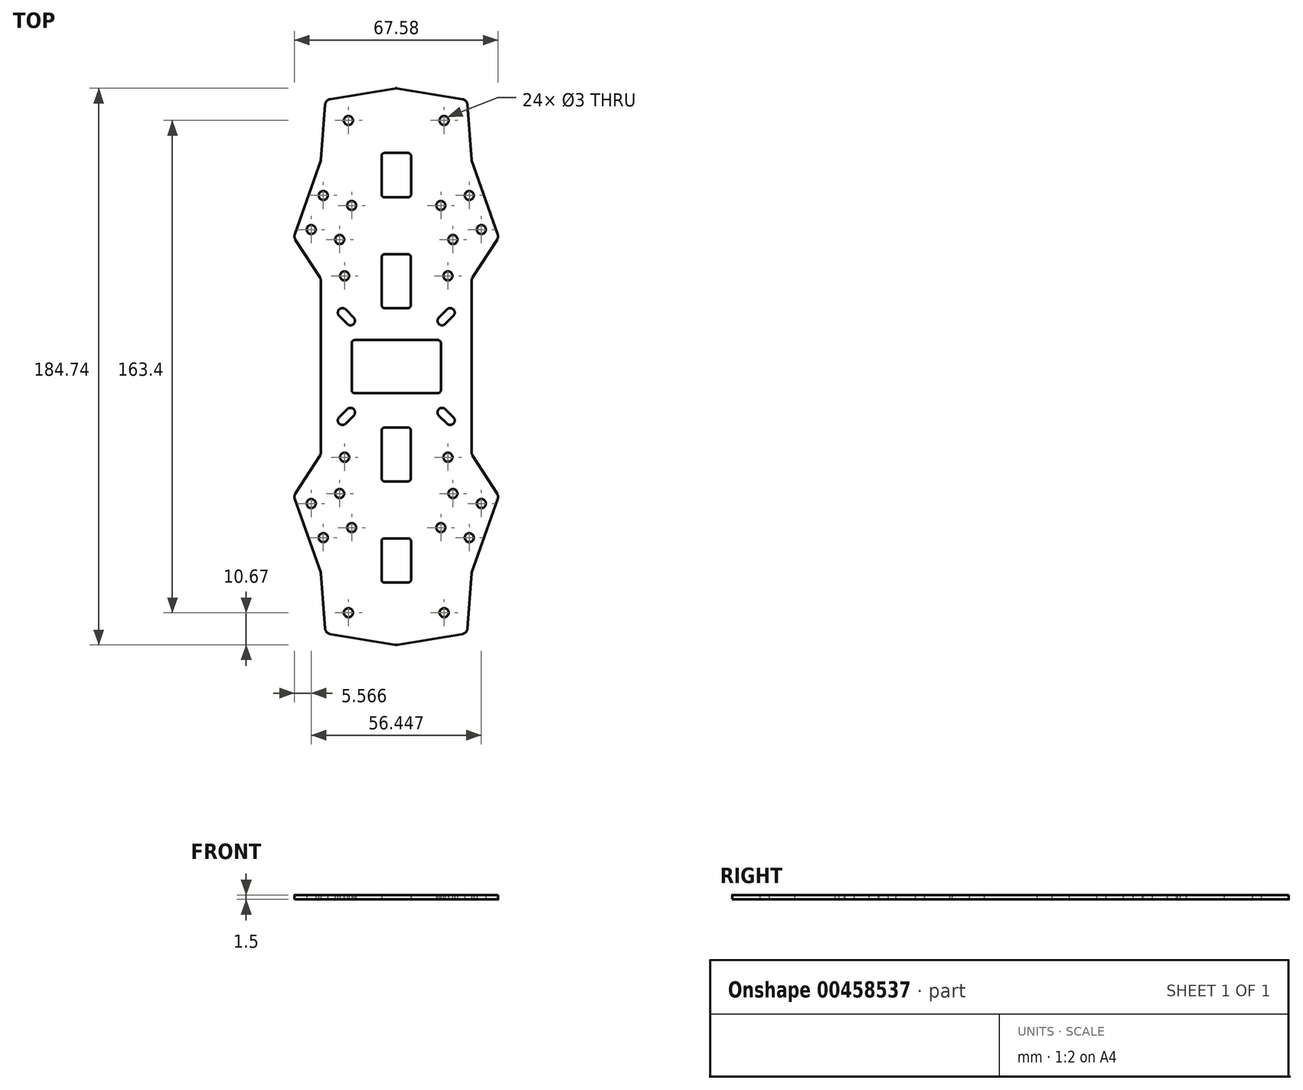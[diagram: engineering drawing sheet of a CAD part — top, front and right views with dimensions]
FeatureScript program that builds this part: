
annotation { "Feature Type Name" : "Feature", "Feature Type Description" : "" }
export const myFeature = defineFeature(function(context is Context, id is Id, definition is map)
    precondition{}
    {
        {
            var Q0;
            Q0=qCreatedBy(makeId("Top.planeOp"),FACE);
            var sketch = newSketch(context, id + "F0", { "sketchPlane" : qUnion([Q0])});
            skLineSegment(sketch, "E0", {"start": v(-25, 28.41) * mm, "end": v(-25, -28.41) * mm});
            skLineSegment(sketch, "E1", {"start": v(-25.32, -29.5) * mm, "end": v(-33.47, -42.18) * mm});
            skLineSegment(sketch, "E2", {"start": v(-33.67, -43.92) * mm, "end": v(-25.04, -68.37) * mm});
            skLineSegment(sketch, "E3", {"start": v(-25, -68.63) * mm, "end": v(-23.62, -86.93) * mm});
            skLineSegment(sketch, "E4", {"start": v(-21.95, -88.76) * mm, "end": v(-0.33, -92.35) * mm});
            skLineSegment(sketch, "E5", {"start": v(0.33, -92.35) * mm, "end": v(21.95, -88.76) * mm});
            skLineSegment(sketch, "E6", {"start": v(23.62, -86.93) * mm, "end": v(25, -68.63) * mm});
            skLineSegment(sketch, "E7", {"start": v(25.04, -68.37) * mm, "end": v(33.67, -43.92) * mm});
            skLineSegment(sketch, "E8", {"start": v(33.47, -42.18) * mm, "end": v(25.32, -29.5) * mm});
            skLineSegment(sketch, "E9", {"start": v(25, -28.41) * mm, "end": v(25, 28.41) * mm});
            skLineSegment(sketch, "E10", {"start": v(25.32, 29.5) * mm, "end": v(33.47, 42.18) * mm});
            skLineSegment(sketch, "E11", {"start": v(33.67, 43.92) * mm, "end": v(25.04, 68.37) * mm});
            skLineSegment(sketch, "E12", {"start": v(25, 68.63) * mm, "end": v(23.62, 86.93) * mm});
            skLineSegment(sketch, "E13", {"start": v(21.95, 88.76) * mm, "end": v(0.33, 92.35) * mm});
            skLineSegment(sketch, "E14", {"start": v(-0.33, 92.35) * mm, "end": v(-21.95, 88.76) * mm});
            skLineSegment(sketch, "E15", {"start": v(-23.62, 86.93) * mm, "end": v(-25, 68.63) * mm});
            skLineSegment(sketch, "E16", {"start": v(-25.04, 68.37) * mm, "end": v(-33.67, 43.92) * mm});
            skLineSegment(sketch, "E17", {"start": v(-33.47, 42.18) * mm, "end": v(-25.32, 29.5) * mm});
            skLineSegment(sketch, "E18.bottom", {"start": v(-13.8, 8.8) * mm, "end": v(13.8, 8.8) * mm});
            skLineSegment(sketch, "E18.top", {"start": v(-13.8, -8.8) * mm, "end": v(13.8, -8.8) * mm});
            skLineSegment(sketch, "E18.left", {"start": v(-14.8, 7.8) * mm, "end": v(-14.8, -7.8) * mm});
            skLineSegment(sketch, "E18.right", {"start": v(14.8, 7.8) * mm, "end": v(14.8, -7.8) * mm});
            skPoint(sketch, "E18.middle", {"position": v(0, 0) * mm});
            skPoint(sketch, "E19.visualSharp", {"position": v(-14.8, 8.8) * mm});
            skArc(sketch, "E19.filletArc", {"start": v(-13.8, 8.8) * mm, "mid": v(-14.5, 8.5) * mm, "end": v(-14.8, 7.8) * mm});
            skPoint(sketch, "E20.visualSharp", {"position": v(14.8, 8.8) * mm});
            skArc(sketch, "E20.filletArc", {"start": v(14.8, 7.8) * mm, "mid": v(14.5, 8.5) * mm, "end": v(13.8, 8.8) * mm});
            skPoint(sketch, "E21.visualSharp", {"position": v(14.8, -8.8) * mm});
            skArc(sketch, "E21.filletArc", {"start": v(13.8, -8.8) * mm, "mid": v(14.5, -8.5) * mm, "end": v(14.8, -7.8) * mm});
            skPoint(sketch, "E22.visualSharp", {"position": v(-14.8, -8.8) * mm});
            skArc(sketch, "E22.filletArc", {"start": v(-14.8, -7.8) * mm, "mid": v(-14.5, -8.5) * mm, "end": v(-13.8, -8.8) * mm});
            skLineSegment(sketch, "E23.bottom", {"start": v(-3.85, 19.4) * mm, "end": v(3.85, 19.4) * mm});
            skLineSegment(sketch, "E23.top", {"start": v(-3.85, 37.3) * mm, "end": v(3.85, 37.3) * mm});
            skLineSegment(sketch, "E23.left", {"start": v(-4.85, 20.4) * mm, "end": v(-4.85, 36.3) * mm});
            skLineSegment(sketch, "E23.right", {"start": v(4.85, 20.4) * mm, "end": v(4.85, 36.3) * mm});
            skPoint(sketch, "E23.middle", {"position": v(0, 28.35) * mm});
            skPoint(sketch, "E24.visualSharp", {"position": v(-4.85, 37.3) * mm});
            skArc(sketch, "E24.filletArc", {"start": v(-3.85, 37.3) * mm, "mid": v(-4.56, 37) * mm, "end": v(-4.85, 36.3) * mm});
            skPoint(sketch, "E25.visualSharp", {"position": v(4.85, 37.3) * mm});
            skArc(sketch, "E25.filletArc", {"start": v(4.85, 36.3) * mm, "mid": v(4.56, 37) * mm, "end": v(3.85, 37.3) * mm});
            skPoint(sketch, "E26.visualSharp", {"position": v(4.85, 19.4) * mm});
            skArc(sketch, "E26.filletArc", {"start": v(3.85, 19.4) * mm, "mid": v(4.56, 19.7) * mm, "end": v(4.85, 20.4) * mm});
            skPoint(sketch, "E27.visualSharp", {"position": v(-4.85, 19.4) * mm});
            skArc(sketch, "E27.filletArc", {"start": v(-4.85, 20.4) * mm, "mid": v(-4.56, 19.7) * mm, "end": v(-3.85, 19.4) * mm});
            skLineSegment(sketch, "E28.bottom", {"start": v(-3.9, 56.2) * mm, "end": v(3.9, 56.2) * mm});
            skLineSegment(sketch, "E28.top", {"start": v(-3.9, 70.9) * mm, "end": v(3.9, 70.9) * mm});
            skLineSegment(sketch, "E28.left", {"start": v(-4.9, 57.2) * mm, "end": v(-4.9, 69.9) * mm});
            skLineSegment(sketch, "E28.right", {"start": v(4.9, 57.2) * mm, "end": v(4.9, 69.9) * mm});
            skPoint(sketch, "E28.middle", {"position": v(0, 63.55) * mm});
            skPoint(sketch, "E29.visualSharp", {"position": v(4.9, 56.2) * mm});
            skArc(sketch, "E29.filletArc", {"start": v(3.9, 56.2) * mm, "mid": v(4.6, 56.5) * mm, "end": v(4.9, 57.2) * mm});
            skPoint(sketch, "E30.visualSharp", {"position": v(-4.9, 56.2) * mm});
            skArc(sketch, "E30.filletArc", {"start": v(-4.9, 57.2) * mm, "mid": v(-4.6, 56.5) * mm, "end": v(-3.9, 56.2) * mm});
            skPoint(sketch, "E31.visualSharp", {"position": v(-4.9, 70.9) * mm});
            skArc(sketch, "E31.filletArc", {"start": v(-3.9, 70.9) * mm, "mid": v(-4.6, 70.6) * mm, "end": v(-4.9, 69.9) * mm});
            skPoint(sketch, "E32.visualSharp", {"position": v(4.9, 70.9) * mm});
            skArc(sketch, "E32.filletArc", {"start": v(4.9, 69.9) * mm, "mid": v(4.6, 70.6) * mm, "end": v(3.9, 70.9) * mm});
            skPoint(sketch, "E33.visualSharp", {"position": v(-34, -43) * mm});
            skArc(sketch, "E33.filletArc", {"start": v(-33.47, -42.18) * mm, "mid": v(-33.77, -43.03) * mm, "end": v(-33.67, -43.92) * mm});
            skPoint(sketch, "E34.visualSharp", {"position": v(34, -43) * mm});
            skArc(sketch, "E34.filletArc", {"start": v(33.67, -43.92) * mm, "mid": v(33.77, -43.03) * mm, "end": v(33.47, -42.18) * mm});
            skPoint(sketch, "E35.visualSharp", {"position": v(25, -29) * mm});
            skArc(sketch, "E35.filletArc", {"start": v(25, -28.41) * mm, "mid": v(25.08, -28.98) * mm, "end": v(25.32, -29.5) * mm});
            skPoint(sketch, "E36.visualSharp", {"position": v(-25, -29) * mm});
            skArc(sketch, "E36.filletArc", {"start": v(-25.32, -29.5) * mm, "mid": v(-25.08, -28.98) * mm, "end": v(-25, -28.41) * mm});
            skPoint(sketch, "E37.visualSharp", {"position": v(-25, -68.5) * mm});
            skArc(sketch, "E37.filletArc", {"start": v(-25, -68.63) * mm, "mid": v(-25, -68.5) * mm, "end": v(-25.04, -68.37) * mm});
            skPoint(sketch, "E38.visualSharp", {"position": v(25, -68.5) * mm});
            skArc(sketch, "E38.filletArc", {"start": v(25.04, -68.37) * mm, "mid": v(25, -68.5) * mm, "end": v(25, -68.63) * mm});
            skPoint(sketch, "E39.visualSharp", {"position": v(23.5, -88.5) * mm});
            skArc(sketch, "E39.filletArc", {"start": v(21.95, -88.76) * mm, "mid": v(23.1, -88.13) * mm, "end": v(23.62, -86.93) * mm});
            skPoint(sketch, "E40.visualSharp", {"position": v(-23.5, -88.5) * mm});
            skArc(sketch, "E40.filletArc", {"start": v(-23.62, -86.93) * mm, "mid": v(-23.1, -88.13) * mm, "end": v(-21.95, -88.76) * mm});
            skPoint(sketch, "E41.visualSharp", {"position": v(0, -92.4) * mm});
            skArc(sketch, "E41.filletArc", {"start": v(-0.33, -92.35) * mm, "mid": v(0, -92.37) * mm, "end": v(0.33, -92.35) * mm});
            skPoint(sketch, "E42.visualSharp", {"position": v(25, 29) * mm});
            skArc(sketch, "E42.filletArc", {"start": v(25.32, 29.5) * mm, "mid": v(25.08, 28.98) * mm, "end": v(25, 28.41) * mm});
            skPoint(sketch, "E43.visualSharp", {"position": v(-25, 29) * mm});
            skArc(sketch, "E43.filletArc", {"start": v(-25, 28.41) * mm, "mid": v(-25.08, 28.98) * mm, "end": v(-25.32, 29.5) * mm});
            skPoint(sketch, "E44.visualSharp", {"position": v(34, 43) * mm});
            skArc(sketch, "E44.filletArc", {"start": v(33.47, 42.18) * mm, "mid": v(33.77, 43.03) * mm, "end": v(33.67, 43.92) * mm});
            skPoint(sketch, "E45.visualSharp", {"position": v(-34, 43) * mm});
            skArc(sketch, "E45.filletArc", {"start": v(-33.67, 43.92) * mm, "mid": v(-33.77, 43.03) * mm, "end": v(-33.47, 42.18) * mm});
            skPoint(sketch, "E46.visualSharp", {"position": v(-25, 68.5) * mm});
            skArc(sketch, "E46.filletArc", {"start": v(-25.04, 68.37) * mm, "mid": v(-25, 68.5) * mm, "end": v(-25, 68.63) * mm});
            skPoint(sketch, "E47.visualSharp", {"position": v(25, 68.5) * mm});
            skArc(sketch, "E47.filletArc", {"start": v(25, 68.63) * mm, "mid": v(25, 68.5) * mm, "end": v(25.04, 68.37) * mm});
            skPoint(sketch, "E48.visualSharp", {"position": v(23.5, 88.5) * mm});
            skArc(sketch, "E48.filletArc", {"start": v(23.62, 86.93) * mm, "mid": v(23.1, 88.13) * mm, "end": v(21.95, 88.76) * mm});
            skPoint(sketch, "E49.visualSharp", {"position": v(-23.5, 88.5) * mm});
            skArc(sketch, "E49.filletArc", {"start": v(-21.95, 88.76) * mm, "mid": v(-23.1, 88.13) * mm, "end": v(-23.62, 86.93) * mm});
            skPoint(sketch, "E50.visualSharp", {"position": v(0, 92.4) * mm});
            skArc(sketch, "E50.filletArc", {"start": v(0.33, 92.35) * mm, "mid": v(0, 92.37) * mm, "end": v(-0.33, 92.35) * mm});
            skArc(sketch, "E51.MirrorCS", {"start": v(4.85, 20.4) * mm, "mid": v(4.56, 19.7) * mm, "end": v(3.85, 19.4) * mm});
            skArc(sketch, "E52.MirrorCS", {"start": v(-3.85, 19.4) * mm, "mid": v(-4.56, 19.7) * mm, "end": v(-4.85, 20.4) * mm});
            skLineSegment(sketch, "E53.MirrorCS", {"start": v(3.85, 19.4) * mm, "end": v(-3.85, 19.4) * mm});
            skCircle(sketch, "E54", {"center": v(-17.15, 30.1) * mm, "radius": 1.5 * mm});
            skCircle(sketch, "E55.MirrorC", {"center": v(-17.15, -30.1) * mm, "radius": 1.5 * mm});
            skCircle(sketch, "E56.MirrorC", {"center": v(17.15, -30.1) * mm, "radius": 1.5 * mm});
            skCircle(sketch, "E57.MirrorC", {"center": v(17.15, 30.1) * mm, "radius": 1.5 * mm});
            skCircle(sketch, "E58", {"center": v(-15.88, 81.7) * mm, "radius": 1.5 * mm});
            skCircle(sketch, "E59.MirrorC", {"center": v(15.88, 81.7) * mm, "radius": 1.5 * mm});
            skCircle(sketch, "E60.MirrorC", {"center": v(15.88, -81.7) * mm, "radius": 1.5 * mm});
            skCircle(sketch, "E61.MirrorC", {"center": v(-15.88, -81.7) * mm, "radius": 1.5 * mm});
            skLineSegment(sketch, "E62", {"start": v(-17.89, 17.89) * mm, "end": v(-15.2, 15.2) * mm});
            skArc(sketch, "E63.0.startCap", {"start": v(-18.95, 16.83) * mm, "mid": v(-18.95, 18.95) * mm, "end": v(-16.83, 18.95) * mm});
            skArc(sketch, "E63.0.endCap", {"start": v(-14.14, 16.26) * mm, "mid": v(-14.14, 14.14) * mm, "end": v(-16.26, 14.14) * mm});
            skLineSegment(sketch, "E63.0.left", {"start": v(-16.83, 18.95) * mm, "end": v(-14.14, 16.26) * mm});
            skLineSegment(sketch, "E63.0.right", {"start": v(-18.95, 16.83) * mm, "end": v(-16.26, 14.14) * mm});
            skLineSegment(sketch, "E64.MirrorCS", {"start": v(18.95, 16.83) * mm, "end": v(16.26, 14.14) * mm});
            skLineSegment(sketch, "E65.MirrorCS", {"start": v(17.89, 17.89) * mm, "end": v(15.2, 15.2) * mm});
            skLineSegment(sketch, "E66.MirrorCS", {"start": v(16.83, 18.95) * mm, "end": v(14.14, 16.26) * mm});
            skArc(sketch, "E67.MirrorCS", {"start": v(18.95, 16.83) * mm, "mid": v(18.95, 18.95) * mm, "end": v(16.83, 18.95) * mm});
            skArc(sketch, "E68.MirrorCS", {"start": v(14.14, 16.26) * mm, "mid": v(14.14, 14.14) * mm, "end": v(16.26, 14.14) * mm});
            skLineSegment(sketch, "E69.MirrorCS", {"start": v(-16.83, -18.95) * mm, "end": v(-14.14, -16.26) * mm});
            skLineSegment(sketch, "E70.MirrorCS", {"start": v(-17.89, -17.89) * mm, "end": v(-15.2, -15.2) * mm});
            skArc(sketch, "E71.MirrorCS", {"start": v(-14.14, -16.26) * mm, "mid": v(-14.14, -14.14) * mm, "end": v(-16.26, -14.14) * mm});
            skLineSegment(sketch, "E72.MirrorCS", {"start": v(-18.95, -16.83) * mm, "end": v(-16.26, -14.14) * mm});
            skArc(sketch, "E73.MirrorCS", {"start": v(-18.95, -16.83) * mm, "mid": v(-18.95, -18.95) * mm, "end": v(-16.83, -18.95) * mm});
            skLineSegment(sketch, "E74.MirrorCS", {"start": v(17.89, -17.89) * mm, "end": v(15.2, -15.2) * mm});
            skLineSegment(sketch, "E75.MirrorCS", {"start": v(18.95, -16.83) * mm, "end": v(16.26, -14.14) * mm});
            skLineSegment(sketch, "E76.MirrorCS", {"start": v(16.83, -18.95) * mm, "end": v(14.14, -16.26) * mm});
            skArc(sketch, "E77.MirrorCS", {"start": v(18.95, -16.83) * mm, "mid": v(18.95, -18.95) * mm, "end": v(16.83, -18.95) * mm});
            skArc(sketch, "E78.MirrorCS", {"start": v(14.14, -16.26) * mm, "mid": v(14.14, -14.14) * mm, "end": v(16.26, -14.14) * mm});
            skLineSegment(sketch, "E79", {"start": v(-24.34, 50.47) * mm, "end": v(-21.51, 49.47) * mm});
            skLineSegment(sketch, "E80", {"start": v(-21.51, 49.47) * mm, "end": v(-20.51, 52.3) * mm});
            skCircle(sketch, "E81", {"center": v(-18.8, 42.15) * mm, "radius": 1.5 * mm});
            skCircle(sketch, "E82.MirrorC", {"center": v(-14.8, 53.47) * mm, "radius": 1.5 * mm});
            skCircle(sketch, "E83.MirrorC", {"center": v(-24.23, 56.8) * mm, "radius": 1.5 * mm});
            skCircle(sketch, "E84.MirrorC", {"center": v(-28.22, 45.48) * mm, "radius": 1.5 * mm});
            skCircle(sketch, "E85.MirrorC", {"center": v(14.8, 53.47) * mm, "radius": 1.5 * mm});
            skCircle(sketch, "E86.MirrorC", {"center": v(24.23, 56.8) * mm, "radius": 1.5 * mm});
            skCircle(sketch, "E87.MirrorC", {"center": v(28.22, 45.48) * mm, "radius": 1.5 * mm});
            skLineSegment(sketch, "E88.MirrorCS", {"start": v(24.34, 50.47) * mm, "end": v(21.51, 49.47) * mm});
            skLineSegment(sketch, "E89.MirrorCS", {"start": v(21.51, 49.47) * mm, "end": v(20.51, 52.3) * mm});
            skCircle(sketch, "E90.MirrorC", {"center": v(18.8, 42.15) * mm, "radius": 1.5 * mm});
            skLineSegment(sketch, "E91.MirrorCS", {"start": v(21.51, -49.47) * mm, "end": v(20.51, -52.3) * mm});
            skLineSegment(sketch, "E92.MirrorCS", {"start": v(24.34, -50.47) * mm, "end": v(21.51, -49.47) * mm});
            skCircle(sketch, "E93.MirrorC", {"center": v(24.23, -56.8) * mm, "radius": 1.5 * mm});
            skCircle(sketch, "E94.MirrorC", {"center": v(28.22, -45.48) * mm, "radius": 1.5 * mm});
            skCircle(sketch, "E95.MirrorC", {"center": v(18.8, -42.15) * mm, "radius": 1.5 * mm});
            skCircle(sketch, "E96.MirrorC", {"center": v(14.8, -53.47) * mm, "radius": 1.5 * mm});
            skCircle(sketch, "E97.MirrorC", {"center": v(-18.8, -42.15) * mm, "radius": 1.5 * mm});
            skCircle(sketch, "E98.MirrorC", {"center": v(-28.22, -45.48) * mm, "radius": 1.5 * mm});
            skLineSegment(sketch, "E99.MirrorCS", {"start": v(-21.51, -49.47) * mm, "end": v(-20.51, -52.3) * mm});
            skLineSegment(sketch, "E100.MirrorCS", {"start": v(-24.34, -50.47) * mm, "end": v(-21.51, -49.47) * mm});
            skCircle(sketch, "E101.MirrorC", {"center": v(-24.23, -56.8) * mm, "radius": 1.5 * mm});
            skCircle(sketch, "E102.MirrorC", {"center": v(-14.8, -53.47) * mm, "radius": 1.5 * mm});
            skLineSegment(sketch, "E103", {"start": v(-5, -0.4) * mm, "end": v(5, -0.4) * mm});
            skArc(sketch, "E104.MirrorCS", {"start": v(4.85, -21.2) * mm, "mid": v(4.56, -20.5) * mm, "end": v(3.85, -20.2) * mm});
            skArc(sketch, "E105.MirrorCS", {"start": v(-3.85, -20.2) * mm, "mid": v(-4.56, -20.5) * mm, "end": v(-4.85, -21.2) * mm});
            skArc(sketch, "E106.MirrorCS", {"start": v(3.85, -20.2) * mm, "mid": v(4.56, -20.5) * mm, "end": v(4.85, -21.2) * mm});
            skArc(sketch, "E107.MirrorCS", {"start": v(-4.85, -21.2) * mm, "mid": v(-4.56, -20.5) * mm, "end": v(-3.85, -20.2) * mm});
            skArc(sketch, "E108.MirrorCS", {"start": v(4.85, -37.1) * mm, "mid": v(4.56, -37.8) * mm, "end": v(3.85, -38.1) * mm});
            skArc(sketch, "E109.MirrorCS", {"start": v(-3.85, -38.1) * mm, "mid": v(-4.56, -37.8) * mm, "end": v(-4.85, -37.1) * mm});
            skLineSegment(sketch, "E110.MirrorCS", {"start": v(-3.85, -20.2) * mm, "end": v(3.85, -20.2) * mm});
            skPoint(sketch, "E111.MirrorP", {"position": v(-4.85, -20.2) * mm});
            skPoint(sketch, "E112.MirrorP", {"position": v(4.85, -20.2) * mm});
            skPoint(sketch, "E113.MirrorP", {"position": v(0, -29.15) * mm});
            skLineSegment(sketch, "E114.MirrorCS", {"start": v(3.85, -20.2) * mm, "end": v(-3.85, -20.2) * mm});
            skLineSegment(sketch, "E115.MirrorCS", {"start": v(-4.85, -21.2) * mm, "end": v(-4.85, -37.1) * mm});
            skLineSegment(sketch, "E116.MirrorCS", {"start": v(-3.85, -38.1) * mm, "end": v(3.85, -38.1) * mm});
            skLineSegment(sketch, "E117.MirrorCS", {"start": v(4.85, -21.2) * mm, "end": v(4.85, -37.1) * mm});
            skPoint(sketch, "E118.MirrorP", {"position": v(-4.85, -38.1) * mm});
            skPoint(sketch, "E119.MirrorP", {"position": v(4.85, -38.1) * mm});
            skArc(sketch, "E120.MirrorCS", {"start": v(3.9, -57) * mm, "mid": v(4.6, -57.3) * mm, "end": v(4.9, -58) * mm});
            skArc(sketch, "E121.MirrorCS", {"start": v(-4.9, -58) * mm, "mid": v(-4.6, -57.3) * mm, "end": v(-3.9, -57) * mm});
            skArc(sketch, "E122.MirrorCS", {"start": v(-3.9, -71.7) * mm, "mid": v(-4.6, -71.4) * mm, "end": v(-4.9, -70.7) * mm});
            skArc(sketch, "E123.MirrorCS", {"start": v(4.9, -70.7) * mm, "mid": v(4.6, -71.4) * mm, "end": v(3.9, -71.7) * mm});
            skLineSegment(sketch, "E124.MirrorCS", {"start": v(-4.9, -58) * mm, "end": v(-4.9, -70.7) * mm});
            skPoint(sketch, "E125.MirrorP", {"position": v(4.9, -71.7) * mm});
            skLineSegment(sketch, "E126.MirrorCS", {"start": v(-3.9, -57) * mm, "end": v(3.9, -57) * mm});
            skPoint(sketch, "E127.MirrorP", {"position": v(-4.9, -71.7) * mm});
            skPoint(sketch, "E128.MirrorP", {"position": v(-4.9, -57) * mm});
            skLineSegment(sketch, "E129.MirrorCS", {"start": v(-3.9, -71.7) * mm, "end": v(3.9, -71.7) * mm});
            skLineSegment(sketch, "E130.MirrorCS", {"start": v(4.9, -58) * mm, "end": v(4.9, -70.7) * mm});
            skPoint(sketch, "E131.MirrorP", {"position": v(0, -64.35) * mm});
            skPoint(sketch, "E132.MirrorP", {"position": v(4.9, -57) * mm});
            skSolve(sketch);
        }
        {
            var Q0;
            Q0=qSketchRegion(id+"F0",true);
            extrude(context, id + "F1", {"entities" : qUnion([Q0]), "depth" : 1.5 * mm});
        }
    });
